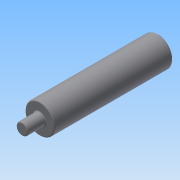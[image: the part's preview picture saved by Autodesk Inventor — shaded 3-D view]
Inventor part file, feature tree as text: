
AUTODESK INVENTOR PART (.ipt)
format: ipt  version: 2015 (Build 190159000, 159)  size: 101,376 bytes
history: native  units: mm
features: extrude x2, fillet x2, sketch x2
ambient origin geometry x8: Origin, YZ Plane, XZ Plane, XY Plane, X Axis, Y Axis, Z Axis, Center Point
bodies: Solid1 (feature_tree)
feature tree (6):
  extrude  "Extrusion1"  Depth=200.0mm TaperAngle=0.0deg
  extrude  "Extrusion2"  Depth=30.0mm TaperAngle=0.0deg
  fillet  "Fillet1"  Radius=2.0mm
  fillet  "Fillet2"  Radius=2.0mm
  sketch  "Sketch2"  dims[d0=50.0mm d1=200.0mm d2=0.0mm]
  sketch  "Sketch3"  dims[d3=20.0mm d4=30.0mm d5=0.0mm d9=2.0mm d10=2.0mm]
